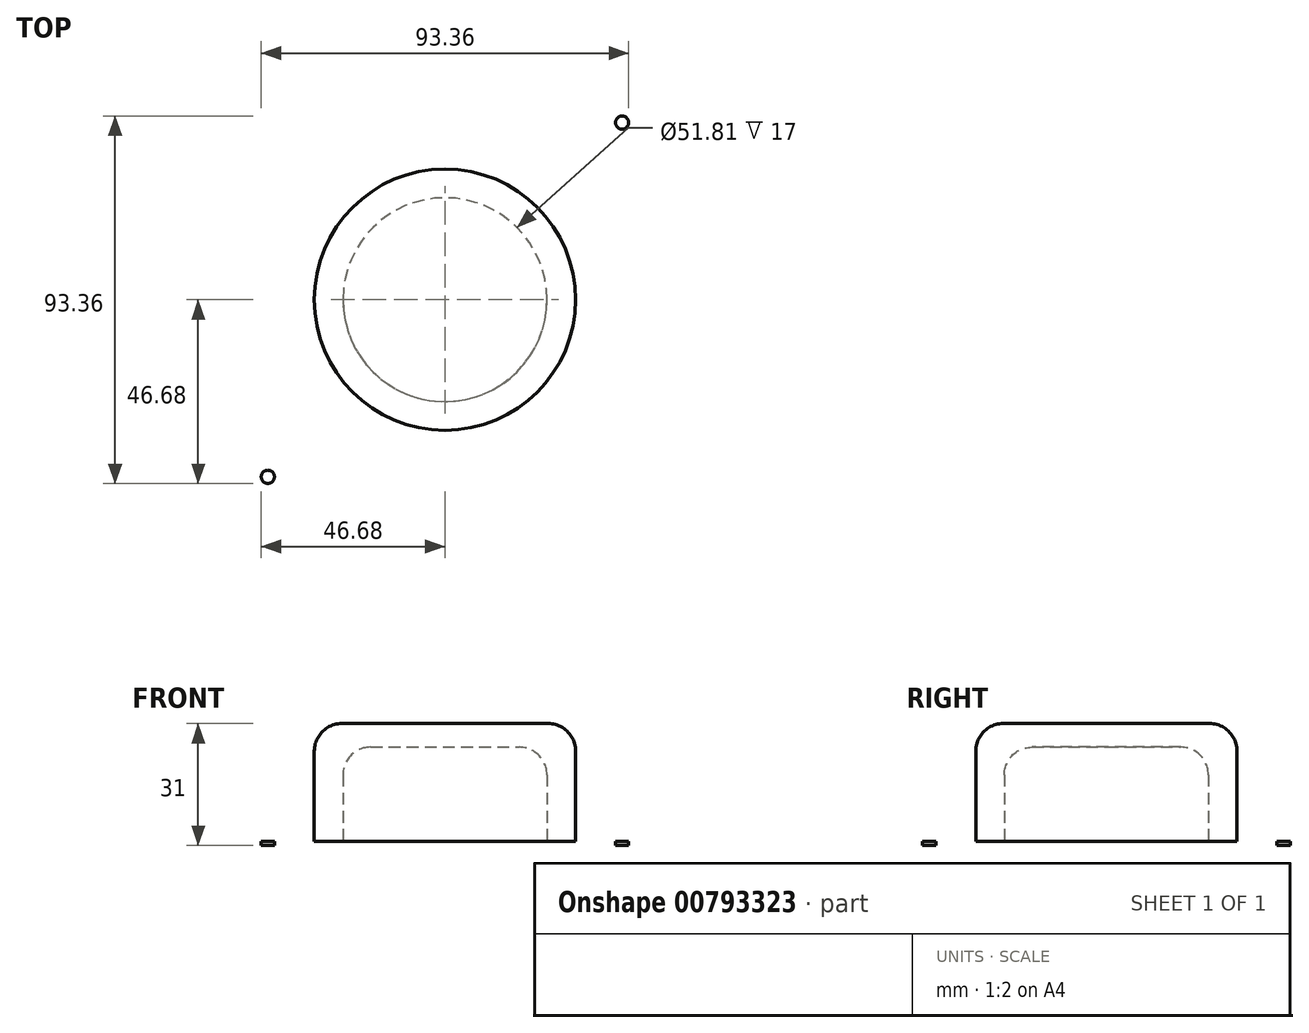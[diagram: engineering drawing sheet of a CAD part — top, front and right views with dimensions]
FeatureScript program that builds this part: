
annotation { "Feature Type Name" : "Feature", "Feature Type Description" : "" }
export const myFeature = defineFeature(function(context is Context, id is Id, definition is map)
    precondition{}
    {
        {
            var Q0;
            Q0=qCreatedBy(makeId("Top.planeOp"),FACE);
            var sketch = newSketch(context, id + "F0", { "sketchPlane" : qUnion([Q0])});
            skLineSegment(sketch, "E0.bottom", {"start": v(50, -50) * mm, "end": v(-50, -50) * mm});
            skLineSegment(sketch, "E0.top", {"start": v(50, 50) * mm, "end": v(-50, 50) * mm});
            skLineSegment(sketch, "E0.left", {"start": v(50, -50) * mm, "end": v(50, 50) * mm});
            skLineSegment(sketch, "E0.right", {"start": v(-50, -50) * mm, "end": v(-50, 50) * mm});
            skPoint(sketch, "E0.middle", {"position": v(0, 0) * mm});
            skSolve(sketch);
        }
        {
            var Q0;
            Q0 = qSketchRegion(id + "F0", true);
            extrude(context, id + "F1", {"entities" : qUnion([Q0]), "depth" : 1 * mm, "offsetDistance" : 25 * mm});
        }
        {
            var Q0;
            Q0=makeQuery(id+"F1.opExtrude","SWEPT_EDGE",EDGE,{"disambiguationData":[OSD([sQuery(id+"F0.wireOp",EDGE,"E0.bottom"),sQuery(id+"F0.wireOp",EDGE,"E0.left")])]});
            var Q1;
            Q1=makeQuery(id+"F1.opExtrude","SWEPT_EDGE",EDGE,{"disambiguationData":[OSD([sQuery(id+"F0.wireOp",EDGE,"E0.bottom"),sQuery(id+"F0.wireOp",EDGE,"E0.right")])]});
            var Q2;
            Q2=makeQuery(id+"F1.opExtrude","SWEPT_EDGE",EDGE,{"disambiguationData":[OSD([sQuery(id+"F0.wireOp",EDGE,"E0.top"),sQuery(id+"F0.wireOp",EDGE,"E0.right")])]});
            var Q3;
            Q3=makeQuery(id+"F1.opExtrude","SWEPT_EDGE",EDGE,{"disambiguationData":[OSD([sQuery(id+"F0.wireOp",EDGE,"E0.top"),sQuery(id+"F0.wireOp",EDGE,"E0.left")])]});
            fillet(context, id + "F2", {"entities" : qUnion([Q0, Q1, Q2, Q3]), "radius" : 5 * mm, "tangentPropagation" : true, "allowEdgeOverflow" : false});
        }
        {
            var Q0;
            Q0=makeQuery(id+"F1.opExtrude","CAP_FACE",FACE,{"disambiguationData":[OSD([sQuery(id+"F0.wireOp",EDGE,"E0.bottom"),sQuery(id+"F0.wireOp",EDGE,"E0.top"),sQuery(id+"F0.wireOp",EDGE,"E0.left"),sQuery(id+"F0.wireOp",EDGE,"E0.right")])],"isStart":false});
            var sketch = newSketch(context, id + "F3", { "sketchPlane" : qUnion([Q0])});
            skCircle(sketch, "E1", {"center": v(-45, 45) * mm, "radius": 1.68 * mm});
            skCircle(sketch, "E2.MirrorC", {"center": v(-45, -45) * mm, "radius": 1.68 * mm});
            skCircle(sketch, "E3.MirrorC", {"center": v(45, 45) * mm, "radius": 1.68 * mm});
            skCircle(sketch, "E4.MirrorC", {"center": v(45, -45) * mm, "radius": 1.68 * mm});
            skSolve(sketch);
        }
        {
            var Q0;
            Q0=makeQuery(id+"F3.imprint","IMPRINT",FACE,{"disambiguationData":[TD([[makeQuery(id+"F3.imprint","IMPRINT",EDGE,{"derivedFrom":sQuery(id+"F3.wireOp",EDGE,"E3.MirrorC")}),-1.0]])]});
            var Q1;
            Q1=makeQuery(id+"F3.imprint","IMPRINT",FACE,{"disambiguationData":[TD([[makeQuery(id+"F3.imprint","IMPRINT",EDGE,{"derivedFrom":sQuery(id+"F3.wireOp",EDGE,"E1")}),1.0]])]});
            var Q2;
            Q2=makeQuery(id+"F3.imprint","IMPRINT",FACE,{"disambiguationData":[TD([[makeQuery(id+"F3.imprint","IMPRINT",EDGE,{"derivedFrom":sQuery(id+"F3.wireOp",EDGE,"E2.MirrorC")}),-1.0]])]});
            var Q3;
            Q3=makeQuery(id+"F3.imprint","IMPRINT",FACE,{"disambiguationData":[TD([[makeQuery(id+"F3.imprint","IMPRINT",EDGE,{"derivedFrom":sQuery(id+"F3.wireOp",EDGE,"E4.MirrorC")}),1.0]])]});
            extrude(context, id + "F4", {"entities" : qUnion([Q0, Q1, Q2, Q3]), "operationType" : NewBodyOperationType.REMOVE, "oppositeDirection" : true, "depth" : 25 * mm, "offsetDistance" : 25 * mm});
        }
        {
            var Q0;
            Q0=makeQuery(id+"F1.opExtrude","CAP_FACE",FACE,{"disambiguationData":[OSD([sQuery(id+"F0.wireOp",EDGE,"E0.bottom"),sQuery(id+"F0.wireOp",EDGE,"E0.top"),sQuery(id+"F0.wireOp",EDGE,"E0.left"),sQuery(id+"F0.wireOp",EDGE,"E0.right")])],"isStart":false});
            var sketch = newSketch(context, id + "F5", { "sketchPlane" : qUnion([Q0])});
            skCircle(sketch, "E5", {"center": v(0, 0) * mm, "radius": 33.19 * mm});
            skSolve(sketch);
        }
        {
            var Q0;
            Q0 = qSketchRegion(id + "F5", true);
            extrude(context, id + "F6", {"entities" : qUnion([Q0]), "operationType" : NewBodyOperationType.ADD, "depth" : 30 * mm, "offsetDistance" : 25 * mm});
        }
        {
            var Q0;
            Q0=makeQuery(id+"F1.opExtrude","CAP_FACE",FACE,{"disambiguationData":[OSD([sQuery(id+"F0.wireOp",EDGE,"E0.bottom"),sQuery(id+"F0.wireOp",EDGE,"E0.top"),sQuery(id+"F0.wireOp",EDGE,"E0.left"),sQuery(id+"F0.wireOp",EDGE,"E0.right")])],"isStart":true});
            var sketch = newSketch(context, id + "F7", { "sketchPlane" : qUnion([Q0])});
            skCircle(sketch, "E6", {"center": v(0, 0) * mm, "radius": 25.9 * mm});
            skSolve(sketch);
        }
        {
            var Q0;
            Q0 = qSketchRegion(id + "F7", true);
            extrude(context, id + "F8", {"entities" : qUnion([Q0]), "operationType" : NewBodyOperationType.REMOVE, "oppositeDirection" : true, "depth" : 25 * mm, "offsetDistance" : 25 * mm});
        }
        {
            var Q0;
            Q0=makeQuery(id+"F6.opExtrude","CAP_EDGE",EDGE,{"disambiguationData":[OSD([sQuery(id+"F5.wireOp",EDGE,"E5")])],"isStart":false});
            var Q1;
            Q1=makeQuery(id+"F8.boolean.opBoolean","COPY",EDGE,{"derivedFrom":makeQuery(id+"F8.opExtrude","CAP_EDGE",EDGE,{"disambiguationData":[OSD([sQuery(id+"F7.wireOp",EDGE,"E6")])],"isStart":false})});
            fillet(context, id + "F9", {"entities" : qUnion([Q0, Q1]), "radius" : 7 * mm, "tangentPropagation" : true, "allowEdgeOverflow" : false});
        }
    });
